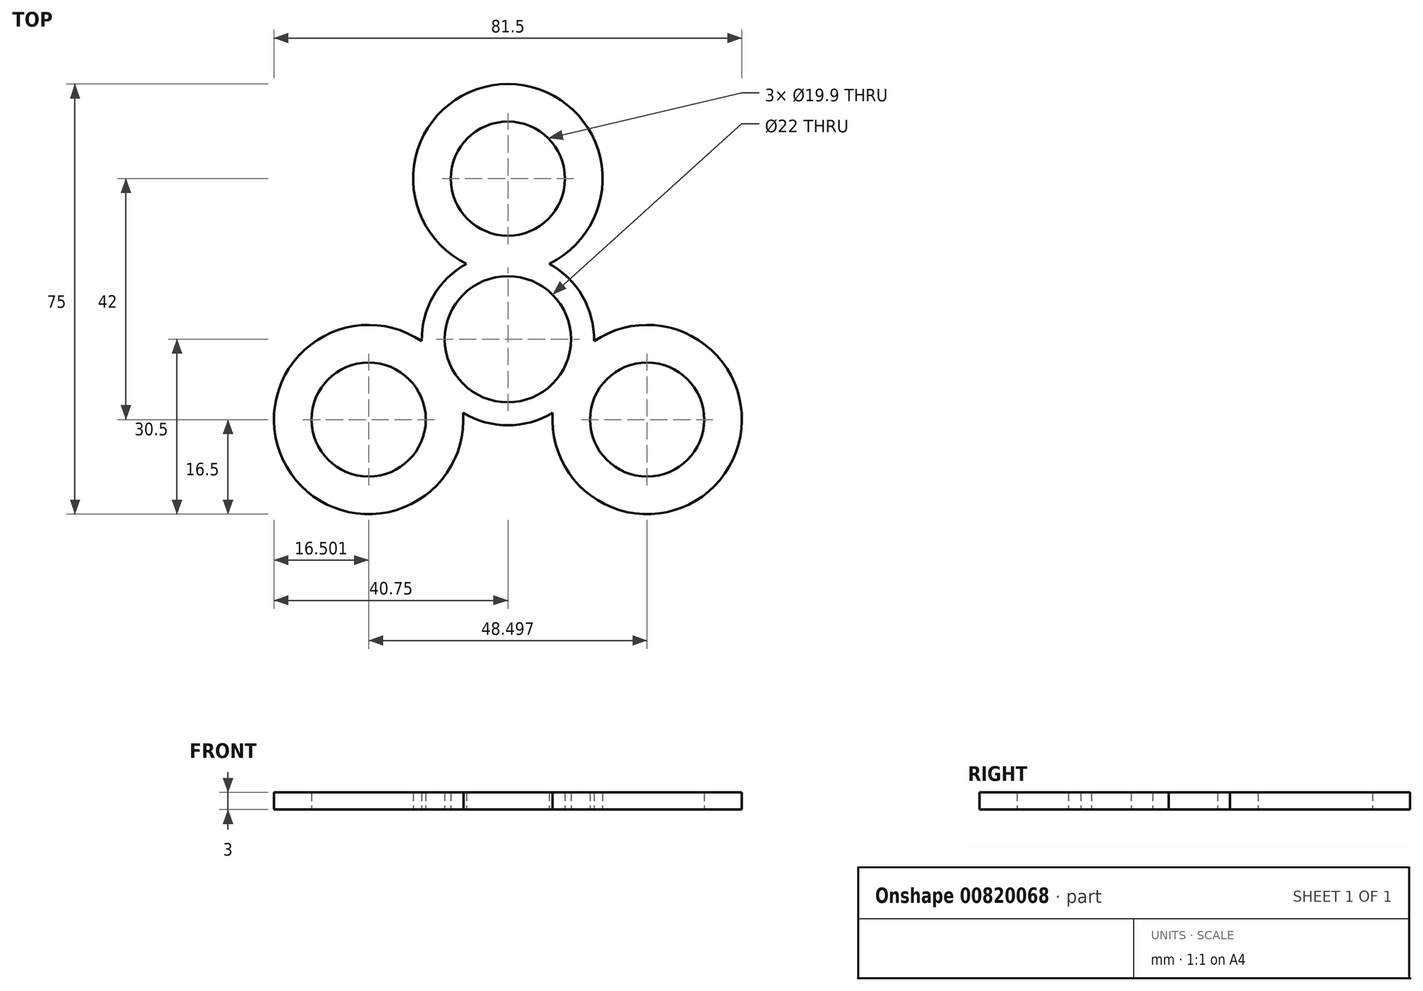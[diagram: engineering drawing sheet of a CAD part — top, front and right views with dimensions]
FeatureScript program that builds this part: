
annotation { "Feature Type Name" : "Feature", "Feature Type Description" : "" }
export const myFeature = defineFeature(function(context is Context, id is Id, definition is map)
    precondition{}
    {
        {
            var Q0;
            Q0=qCreatedBy(makeId("Top.planeOp"),FACE);
            var sketch = newSketch(context, id + "F0", { "sketchPlane" : qUnion([Q0])});
            skCircle(sketch, "E0", {"center": v(0, 0) * mm, "radius": 11 * mm});
            skArc(sketch, "E1", {"start": v(-7.2, 13.16) * mm, "mid": v(-13, 7.5) * mm, "end": v(-15, -0.34) * mm});
            skLineSegment(sketch, "E2", {"start": v(0, 0) * mm, "end": v(0, 28) * mm});
            skCircle(sketch, "E3", {"center": v(0, 28) * mm, "radius": 9.95 * mm});
            skArc(sketch, "E4", {"start": v(7.2, 13.16) * mm, "mid": v(0, 44.5) * mm, "end": v(-7.2, 13.16) * mm});
            skCircle(sketch, "E5.1.0", {"center": v(-24.25, -14) * mm, "radius": 9.95 * mm});
            skArc(sketch, "E5.1.1", {"start": v(-15, -0.34) * mm, "mid": v(-38.54, -22.25) * mm, "end": v(-7.8, -12.82) * mm});
            skCircle(sketch, "E5.2.0", {"center": v(24.25, -14) * mm, "radius": 9.95 * mm});
            skArc(sketch, "E5.2.1", {"start": v(7.8, -12.82) * mm, "mid": v(38.54, -22.25) * mm, "end": v(15, -0.34) * mm});
            skArc(sketch, "E6.trimOffspring", {"start": v(-7.8, -12.82) * mm, "mid": v(0, -15) * mm, "end": v(7.8, -12.82) * mm});
            skArc(sketch, "E7.trimOffspring", {"start": v(15, -0.34) * mm, "mid": v(13, 7.5) * mm, "end": v(7.2, 13.16) * mm});
            skSolve(sketch);
        }
        {
            var Q0;
            Q0 = qSketchRegion(id + "F0", true);
            extrude(context, id + "F1", {"entities" : qUnion([Q0]), "depth" : 3 * mm, "offsetDistance" : 25 * mm});
        }
    });
